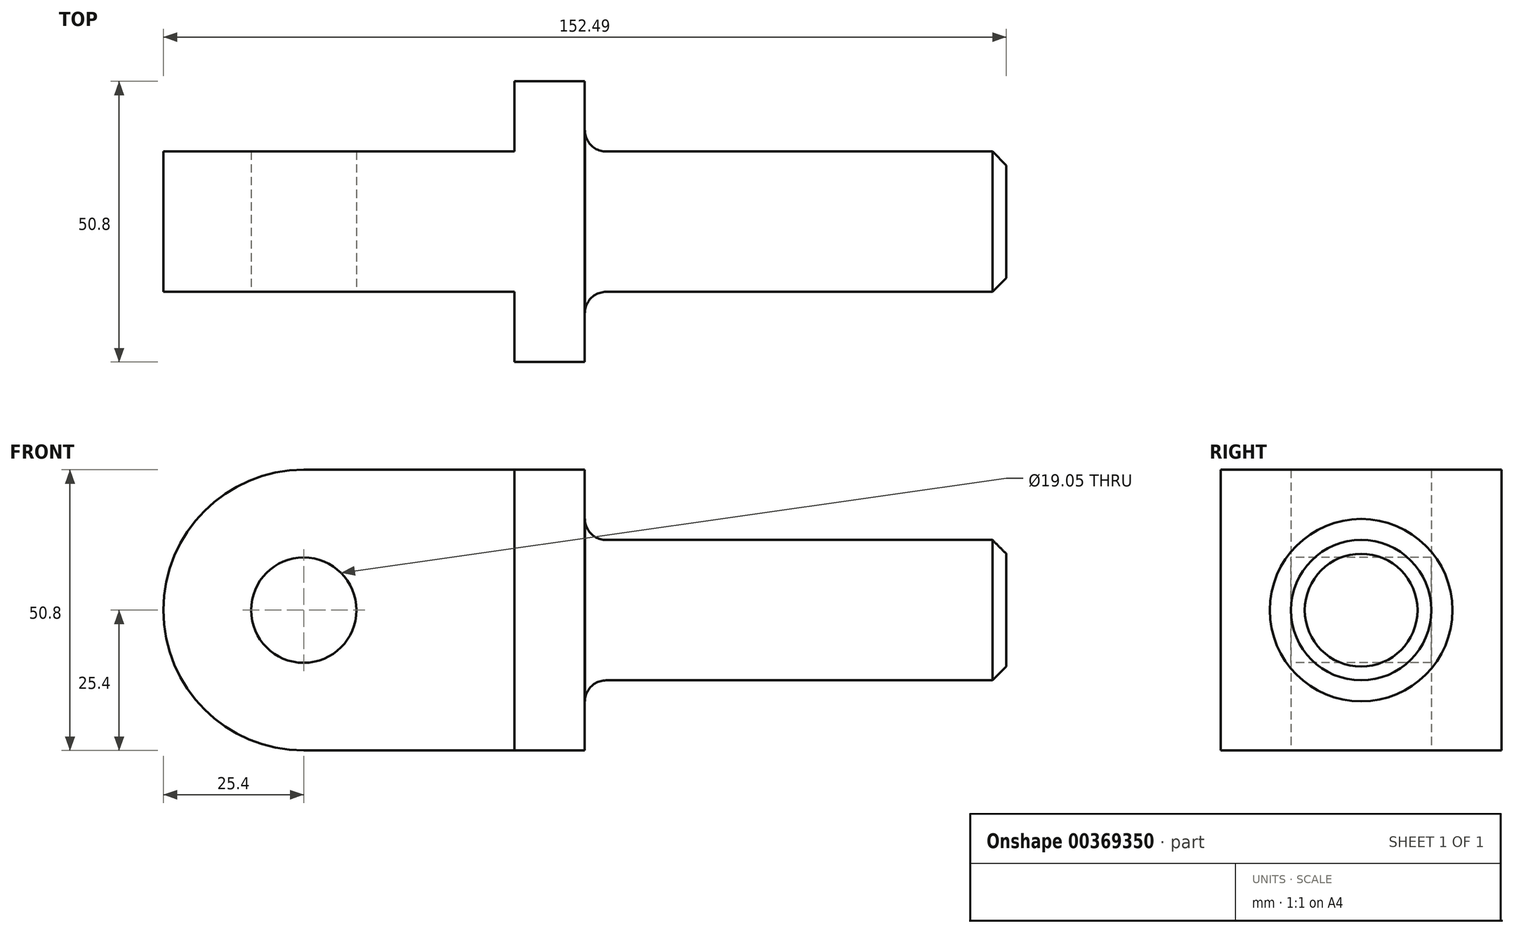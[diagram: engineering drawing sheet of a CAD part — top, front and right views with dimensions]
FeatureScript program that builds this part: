
annotation { "Feature Type Name" : "Feature", "Feature Type Description" : "" }
export const myFeature = defineFeature(function(context is Context, id is Id, definition is map)
    precondition{}
    {
        {
            var Q0;
            Q0=qCreatedBy(makeId("Front.planeOp"),FACE);
            var sketch = newSketch(context, id + "F0", { "sketchPlane" : qUnion([Q0])});
            skLineSegment(sketch, "E0", {"start": v(-9.86, 0) * mm, "end": v(0, 0) * mm, "construction": true});
            skLineSegment(sketch, "E1", {"start": v(3.88, 12.7) * mm, "end": v(73.79, 12.7) * mm});
            skLineSegment(sketch, "E2", {"start": v(49.95, 0) * mm, "end": v(0, 0) * mm});
            skLineSegment(sketch, "E3", {"start": v(73.79, 12.7) * mm, "end": v(76.29, 10.2) * mm});
            skLineSegment(sketch, "E4", {"start": v(76.29, 10.2) * mm, "end": v(76.29, 0) * mm});
            skLineSegment(sketch, "E5", {"start": v(76.29, 0) * mm, "end": v(49.95, 0) * mm});
            skPoint(sketch, "E6.newPointA", {"position": v(0.09, 12.7) * mm});
            skArc(sketch, "E6.filletArc", {"start": v(0.07, 16.51) * mm, "mid": v(1.18, 13.82) * mm, "end": v(3.88, 12.7) * mm});
            skLineSegment(sketch, "E7", {"start": v(0, 0) * mm, "end": v(0.07, 16.51) * mm});
            skPoint(sketch, "E8", {"position": v(24.97, 0) * mm});
            skSolve(sketch);
        }
        {
            var Q0;
            Q0=qCreatedBy(makeId("Front.planeOp"),FACE);
            var sketch = newSketch(context, id + "F1", { "sketchPlane" : qUnion([Q0])});
            skLineSegment(sketch, "E9", {"start": v(0, 25.4) * mm, "end": v(-12.7, 25.4) * mm});
            skLineSegment(sketch, "E10", {"start": v(-12.7, 25.4) * mm, "end": v(-12.7, -25.4) * mm});
            skLineSegment(sketch, "E11", {"start": v(-12.7, -25.4) * mm, "end": v(0, -25.4) * mm});
            skLineSegment(sketch, "E12", {"start": v(0, -25.4) * mm, "end": v(0, 25.4) * mm});
            skPoint(sketch, "E13", {"position": v(-12.7, 0) * mm});
            skSolve(sketch);
        }
        {
            var Q0;
            Q0=makeQuery(id+"F1.imprint","IMPRINT",FACE,{"disambiguationData":[TD([[makeQuery(id+"F1.imprint","IMPRINT",EDGE,{"derivedFrom":sQuery(id+"F1.wireOp",EDGE,"E9")}),1.0]])]});
            extrude(context, id + "F2", {"entities" : qUnion([Q0]), "endBound" : BoundingType.SYMMETRIC, "depth" : 50.8 * mm});
        }
        {
            var Q0;
            Q0 = qSketchRegion(id + "F0", true);
            var Q1;
            Q1=sQuery(id+"F0.wireOp",EDGE,"E0");
            revolve(context, id + "F3", {"operationType" : NewBodyOperationType.ADD, "entities" : qUnion([Q0]), "axis" : qUnion([Q1]), "revolveType" : RevolveType.FULL});
        }
        {
            var Q0;
            Q0=makeQuery(id+"F2.opExtrude","SWEPT_FACE",FACE,{"disambiguationData":[OSD([sQuery(id+"F1.wireOp",EDGE,"E10")])]});
            var sketch = newSketch(context, id + "F4", { "sketchPlane" : qUnion([Q0])});
            skLineSegment(sketch, "E14", {"start": v(-12.7, 25.4) * mm, "end": v(12.7, 25.4) * mm});
            skLineSegment(sketch, "E15", {"start": v(12.7, 25.4) * mm, "end": v(12.7, -25.4) * mm});
            skLineSegment(sketch, "E16", {"start": v(12.7, -25.4) * mm, "end": v(-12.7, -25.4) * mm});
            skLineSegment(sketch, "E17", {"start": v(-12.7, -25.4) * mm, "end": v(-12.7, 25.4) * mm});
            skPoint(sketch, "E18", {"position": v(0, 25.4) * mm});
            skPoint(sketch, "E19", {"position": v(0, -25.4) * mm});
            skSolve(sketch);
        }
        {
            var Q0;
            Q0 = qSketchRegion(id + "F4", true);
            extrude(context, id + "F5", {"entities" : qUnion([Q0]), "operationType" : NewBodyOperationType.ADD, "depth" : 38.1 * mm});
        }
        {
            var Q0;
            Q0=makeQuery(id+"F5.opExtrude","SWEPT_FACE",FACE,{"disambiguationData":[OSD([sQuery(id+"F4.wireOp",EDGE,"E15")])]});
            var sketch = newSketch(context, id + "F6", { "sketchPlane" : qUnion([Q0])});
            skArc(sketch, "E20", {"start": v(-50.8, 25.4) * mm, "mid": v(-76.2, 0) * mm, "end": v(-50.8, -25.4) * mm});
            skCircle(sketch, "E21", {"center": v(-50.8, 0) * mm, "radius": 9.53 * mm});
            skLineSegment(sketch, "E22", {"start": v(-50.8, 25.4) * mm, "end": v(-50.8, -25.4) * mm});
            skSolve(sketch);
        }
        {
            var Q0;
            Q0 = qSketchRegion(id + "F6", true);
            extrude(context, id + "F7", {"entities" : qUnion([Q0]), "operationType" : NewBodyOperationType.ADD, "oppositeDirection" : true, "depth" : 25.4 * mm});
        }
        {
            var Q0;
            {var subQ0=sQuery(id+"F6.wireOp",EDGE,"E22");var subQ1=sQuery(id+"F6.wireOp",EDGE,"E21");var subQ2=makeQuery(id+"F6.imprint","INTERSECT",VERTEX,{"disambiguationData":[OD(0.0)],"derivedFrom":[subQ1,subQ0]});Q0=makeQuery(id+"F6.imprint","IMPRINT",FACE,{"disambiguationData":[TD([[makeQuery(id+"F6.imprint","IMPRINT",EDGE,{"disambiguationData":[TD([[subQ2,1.0]])],"derivedFrom":subQ1}),1.0]])]});}
            var Q1;
            {var subQ0=sQuery(id+"F6.wireOp",EDGE,"E22");var subQ1=sQuery(id+"F6.wireOp",EDGE,"E21");var subQ2=makeQuery(id+"F6.imprint","INTERSECT",VERTEX,{"disambiguationData":[OD(0.0)],"derivedFrom":[subQ1,subQ0]});Q1=makeQuery(id+"F6.imprint","IMPRINT",FACE,{"disambiguationData":[TD([[makeQuery(id+"F6.imprint","IMPRINT",EDGE,{"disambiguationData":[TD([[subQ2,-1.0]])],"derivedFrom":subQ1}),1.0]])]});}
            extrude(context, id + "F8", {"entities" : qUnion([Q0, Q1]), "operationType" : NewBodyOperationType.REMOVE, "oppositeDirection" : true, "depth" : 25.4 * mm});
        }
    });
